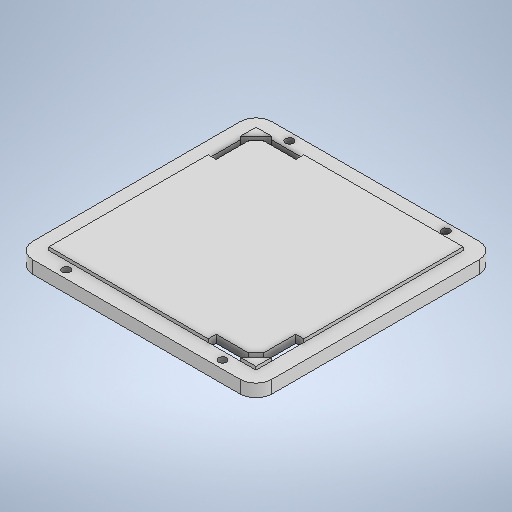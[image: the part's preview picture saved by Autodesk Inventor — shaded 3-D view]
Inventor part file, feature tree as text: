
AUTODESK INVENTOR PART (.ipt)
format: ipt  version: 2025.2 (Build 292293000, 293)  size: 322,560 bytes
history: native  units: mm
features: extrude x6, sketch x6, thread x4, other x1
ambient origin geometry x8: Origin, YZ Plane, XZ Plane, XY Plane, X Axis, Y Axis, Z Axis, Center Point
bodies: Body1 (feature_tree)
feature tree (17):
  other  "Sólido1"
  extrude  "Extrusão1"  Depth=75.0mm
  extrude  "Extrusão2"  Depth=5.0mm TaperAngle=0.0deg
  extrude  "Extrusão3"  Depth=2.5mm
  sketch  "Esboço4"  dims[d7=2.5mm d8=2.5mm]
  extrude  "Extrusão4"  Depth=2.5mm
  extrude  "Extrusão5"  Depth=2.5mm
  extrude  "Extrusão6"  TaperAngle=0.0deg  [1 undecoded]
  thread  "Rosca1"  [1 undecoded]
  thread  "Rosca2"  [1 undecoded]
  thread  "Rosca3"  [1 undecoded]
  thread  "Rosca4"  [1 undecoded]
  sketch  "Esboço1"  dims[d0=75.0mm d1=75.0mm]
  sketch  "Esboço2"  dims[d2=5.0mm d3=5.0mm d4=0.0mm]
  sketch  "Esboço3"  dims[d5=13.0mm d6=2.5mm]
  sketch  "Esboço5"  dims[d9=2.5mm d10=2.5mm]
  sketch  "Esboço6"  dims[d11=2.5mm d12=0.0mm d13=0.0mm d14=5.0mm d15=65.0mm d16=65.0mm d17=2.5mm d18=0.0mm d23=2.5mm d24=10.0mm d25=2.5mm d26=2.5mm d27=0.0mm d28=0.0mm d29=0.0mm d30=1.0mm d31=0.0mm d32=11.0mm d33=0.0mm d34=11.0mm d35=0.0mm d36=11.0mm d37=0.0mm d38=11.0mm d39=0.0mm]
note: 5 required parameter values undecoded (feature->parameter linkage not recoverable at this tier; creation-order binding heuristic only, values carry confidence <= 0.55)
